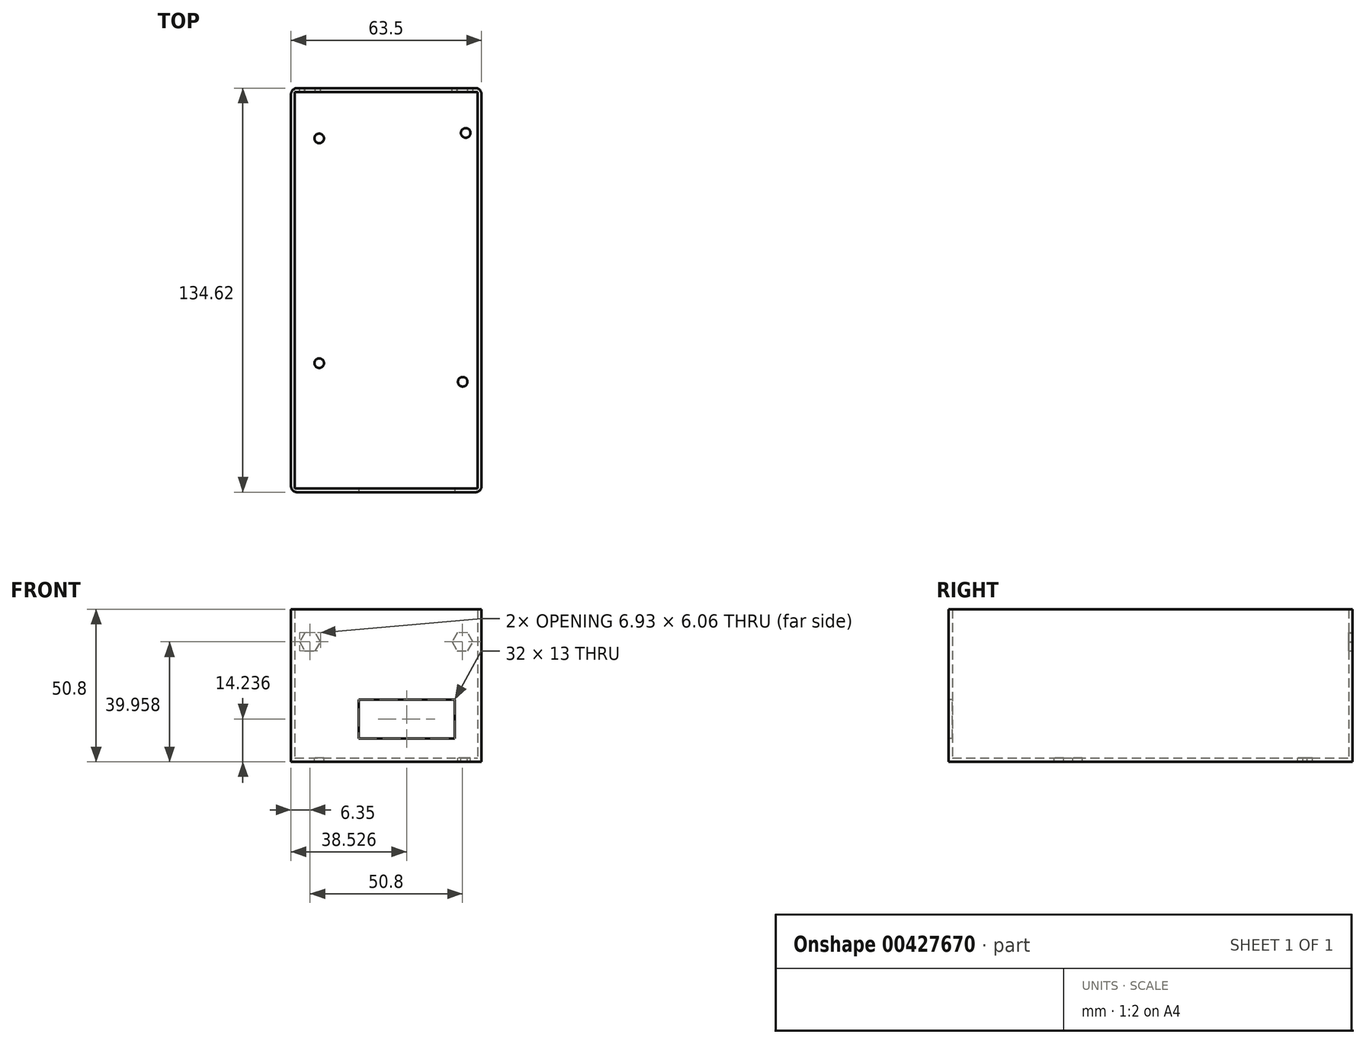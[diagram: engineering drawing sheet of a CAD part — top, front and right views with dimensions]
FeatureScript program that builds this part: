
annotation { "Feature Type Name" : "Feature", "Feature Type Description" : "" }
export const myFeature = defineFeature(function(context is Context, id is Id, definition is map)
    precondition{}
    {
        {
            var Q0;
            Q0=qCreatedBy(makeId("Front.planeOp"),FACE);
            var sketch = newSketch(context, id + "F0", { "sketchPlane" : qUnion([Q0])});
            skLineSegment(sketch, "E0.bottom", {"start": v(-31.75, 25.4) * mm, "end": v(31.75, 25.4) * mm});
            skLineSegment(sketch, "E0.top", {"start": v(-31.75, -25.4) * mm, "end": v(31.75, -25.4) * mm});
            skLineSegment(sketch, "E0.left", {"start": v(-31.75, 25.4) * mm, "end": v(-31.75, -25.4) * mm});
            skLineSegment(sketch, "E0.right", {"start": v(31.75, 25.4) * mm, "end": v(31.75, -25.4) * mm});
            skPoint(sketch, "E0.middle", {"position": v(0, 0) * mm});
            skSolve(sketch);
        }
        {
            var Q0;
            Q0=makeQuery(id+"F0.imprint","IMPRINT",FACE,{"disambiguationData":[TD([[makeQuery(id+"F0.imprint","IMPRINT",EDGE,{"derivedFrom":sQuery(id+"F0.wireOp",EDGE,"E0.bottom")}),-1.0]])]});
            extrude(context, id + "F1", {"entities" : qUnion([Q0]), "depth" : 134.62 * mm});
        }
        {
            var Q0;
            Q0=makeQuery(id+"F1.opExtrude","SWEPT_FACE",FACE,{"disambiguationData":[OSD([sQuery(id+"F0.wireOp",EDGE,"E0.bottom")])]});
            shell(context, id + "F2", {"entities" : qUnion([Q0]), "thickness" : 1.27 * mm});
        }
        {
            var Q0;
            Q0=makeQuery(id+"F1.opExtrude","CAP_FACE",FACE,{"disambiguationData":[OSD([sQuery(id+"F0.wireOp",EDGE,"E0.bottom"),sQuery(id+"F0.wireOp",EDGE,"E0.top"),sQuery(id+"F0.wireOp",EDGE,"E0.left"),sQuery(id+"F0.wireOp",EDGE,"E0.right")])],"isStart":false});
            var sketch = newSketch(context, id + "F3", { "sketchPlane" : qUnion([Q0])});
            skLineSegment(sketch, "E1.bottom", {"start": v(22.78, -17.66) * mm, "end": v(-9.22, -17.66) * mm});
            skLineSegment(sketch, "E1.top", {"start": v(22.78, -4.66) * mm, "end": v(-9.22, -4.66) * mm});
            skLineSegment(sketch, "E1.left", {"start": v(22.78, -17.66) * mm, "end": v(22.78, -4.66) * mm});
            skLineSegment(sketch, "E1.right", {"start": v(-9.22, -17.66) * mm, "end": v(-9.22, -4.66) * mm});
            skPoint(sketch, "E1.middle", {"position": v(6.78, -11.16) * mm});
            skSolve(sketch);
        }
        {
            var Q0;
            Q0=makeQuery(id+"F3.imprint","IMPRINT",FACE,{"disambiguationData":[TD([[makeQuery(id+"F3.imprint","IMPRINT",EDGE,{"derivedFrom":sQuery(id+"F3.wireOp",EDGE,"E1.bottom")}),-1.0]])]});
            extrude(context, id + "F4", {"entities" : qUnion([Q0]), "operationType" : NewBodyOperationType.REMOVE, "oppositeDirection" : true, "depth" : 25.4 * mm});
        }
        {
            var Q0;
            Q0=makeQuery(id+"F1.opExtrude","CAP_FACE",FACE,{"disambiguationData":[OSD([sQuery(id+"F0.wireOp",EDGE,"E0.bottom"),sQuery(id+"F0.wireOp",EDGE,"E0.top"),sQuery(id+"F0.wireOp",EDGE,"E0.left"),sQuery(id+"F0.wireOp",EDGE,"E0.right")])],"isStart":true});
            var sketch = newSketch(context, id + "F5", { "sketchPlane" : qUnion([Q0])});
            skCircle(sketch, "E2.cCircle", {"center": v(-25.4, 14.56) * mm, "radius": 3.46 * mm, "construction": true});
            skLineSegment(sketch, "E2.0", {"start": v(-23.72, 17.59) * mm, "end": v(-21.94, 14.62) * mm});
            skLineSegment(sketch, "E2.1", {"start": v(-21.94, 14.62) * mm, "end": v(-23.62, 11.59) * mm});
            skLineSegment(sketch, "E2.2", {"start": v(-23.62, 11.59) * mm, "end": v(-27.08, 11.53) * mm});
            skLineSegment(sketch, "E2.3", {"start": v(-27.08, 11.53) * mm, "end": v(-28.86, 14.5) * mm});
            skLineSegment(sketch, "E2.4", {"start": v(-28.86, 14.5) * mm, "end": v(-27.18, 17.53) * mm});
            skLineSegment(sketch, "E2.5", {"start": v(-27.18, 17.53) * mm, "end": v(-23.72, 17.59) * mm});
            skCircle(sketch, "E3.1.0.0", {"center": v(25.4, 14.56) * mm, "radius": 3.46 * mm, "construction": true});
            skLineSegment(sketch, "E3.1.0.1", {"start": v(23.72, 11.53) * mm, "end": v(21.94, 14.5) * mm});
            skLineSegment(sketch, "E3.1.0.2", {"start": v(27.18, 11.59) * mm, "end": v(23.72, 11.53) * mm});
            skLineSegment(sketch, "E3.1.0.3", {"start": v(21.94, 14.5) * mm, "end": v(23.62, 17.53) * mm});
            skLineSegment(sketch, "E3.1.0.4", {"start": v(23.62, 17.53) * mm, "end": v(27.08, 17.59) * mm});
            skLineSegment(sketch, "E3.1.0.5", {"start": v(27.08, 17.59) * mm, "end": v(28.86, 14.62) * mm});
            skLineSegment(sketch, "E3.1.0.6", {"start": v(28.86, 14.62) * mm, "end": v(27.18, 11.59) * mm});
            skLineSegment(sketch, "E3.direction1", {"start": v(-25.4, 14.56) * mm, "end": v(25.4, 14.56) * mm, "construction": true});
            skSolve(sketch);
        }
        {
            var Q0;
            Q0=makeQuery(id+"F2.opShell","OFFSET_FACE",FACE,{"disambiguationData":[OSD([sQuery(id+"F0.wireOp",EDGE,"E0.top")])]});
            var sketch = newSketch(context, id + "F6", { "sketchPlane" : qUnion([Q0])});
            skPoint(sketch, "E4", {"position": v(-22.34, -91.63) * mm});
            skPoint(sketch, "E5", {"position": v(25.47, -97.83) * mm});
            skPoint(sketch, "E6", {"position": v(-22.34, -16.73) * mm});
            skPoint(sketch, "E7", {"position": v(26.48, -14.93) * mm});
            skCircle(sketch, "E8", {"center": v(-22.34, -16.73) * mm, "radius": 1.6 * mm});
            skCircle(sketch, "E9", {"center": v(26.48, -14.93) * mm, "radius": 1.6 * mm});
            skCircle(sketch, "E10", {"center": v(-22.34, -91.63) * mm, "radius": 1.6 * mm});
            skCircle(sketch, "E11", {"center": v(25.47, -97.83) * mm, "radius": 1.6 * mm});
            skSolve(sketch);
        }
        {
            var Q0;
            Q0=makeQuery(id+"F6.imprint","IMPRINT",FACE,{"disambiguationData":[TD([[makeQuery(id+"F6.imprint","IMPRINT",EDGE,{"derivedFrom":sQuery(id+"F6.wireOp",EDGE,"E8")}),1.0]])]});
            var Q1;
            {var subQ0=sQuery(id+"F6.wireOp",EDGE,"E9");var subQ1=makeQuery(id+"F2.opShell","OFFSET_EDGE",EDGE,{"disambiguationData":[OSD([sQuery(id+"F0.wireOp",EDGE,"E0.top"),sQuery(id+"F0.wireOp",EDGE,"E0.right")])]});var subQ2=makeQuery(id+"F6.imprint","INTERSECT",VERTEX,{"disambiguationData":[OD(0.0)],"derivedFrom":[subQ1,subQ0]});Q1=makeQuery(id+"F6.imprint","IMPRINT",FACE,{"disambiguationData":[TD([[makeQuery(id+"F6.imprint","IMPRINT",EDGE,{"disambiguationData":[TD([[subQ2,-1.0]])],"derivedFrom":subQ0}),1.0]])]});}
            var Q2;
            Q2=makeQuery(id+"F6.imprint","IMPRINT",FACE,{"disambiguationData":[TD([[makeQuery(id+"F6.imprint","IMPRINT",EDGE,{"derivedFrom":sQuery(id+"F6.wireOp",EDGE,"E10")}),1.0]])]});
            var Q3;
            Q3=makeQuery(id+"F6.imprint","IMPRINT",FACE,{"disambiguationData":[TD([[makeQuery(id+"F6.imprint","IMPRINT",EDGE,{"derivedFrom":sQuery(id+"F6.wireOp",EDGE,"E11")}),1.0]])]});
            extrude(context, id + "F7", {"entities" : qUnion([Q0, Q1, Q2, Q3]), "operationType" : NewBodyOperationType.REMOVE, "oppositeDirection" : true, "depth" : 25.4 * mm});
        }
        {
            var Q0;
            Q0=makeQuery(id+"F1.opExtrude","CAP_EDGE",EDGE,{"disambiguationData":[OSD([sQuery(id+"F0.wireOp",EDGE,"E0.left")])],"isStart":false});
            fillet(context, id + "F8", {"entities" : qUnion([Q0]), "radius" : 2.03 * mm, "tangentPropagation" : true, "allowEdgeOverflow" : false});
        }
        {
            var Q0;
            Q0=makeQuery(id+"F1.opExtrude","CAP_EDGE",EDGE,{"disambiguationData":[OSD([sQuery(id+"F0.wireOp",EDGE,"E0.right")])],"isStart":false});
            fillet(context, id + "F9", {"entities" : qUnion([Q0]), "radius" : 2.03 * mm, "tangentPropagation" : true, "allowEdgeOverflow" : false});
        }
        {
            var Q0;
            Q0=makeQuery(id+"F1.opExtrude","CAP_EDGE",EDGE,{"disambiguationData":[OSD([sQuery(id+"F0.wireOp",EDGE,"E0.right")])],"isStart":true});
            var Q1;
            Q1=makeQuery(id+"F1.opExtrude","CAP_EDGE",EDGE,{"disambiguationData":[OSD([sQuery(id+"F0.wireOp",EDGE,"E0.left")])],"isStart":true});
            fillet(context, id + "F10", {"entities" : qUnion([Q0, Q1]), "radius" : 2.03 * mm, "tangentPropagation" : true, "allowEdgeOverflow" : false});
        }
        {
            var Q0;
            Q0 = qSketchRegion(id + "F5", true);
            extrude(context, id + "F11", {"entities" : qUnion([Q0]), "operationType" : NewBodyOperationType.REMOVE, "oppositeDirection" : true, "depth" : 25.4 * mm});
        }
    });
